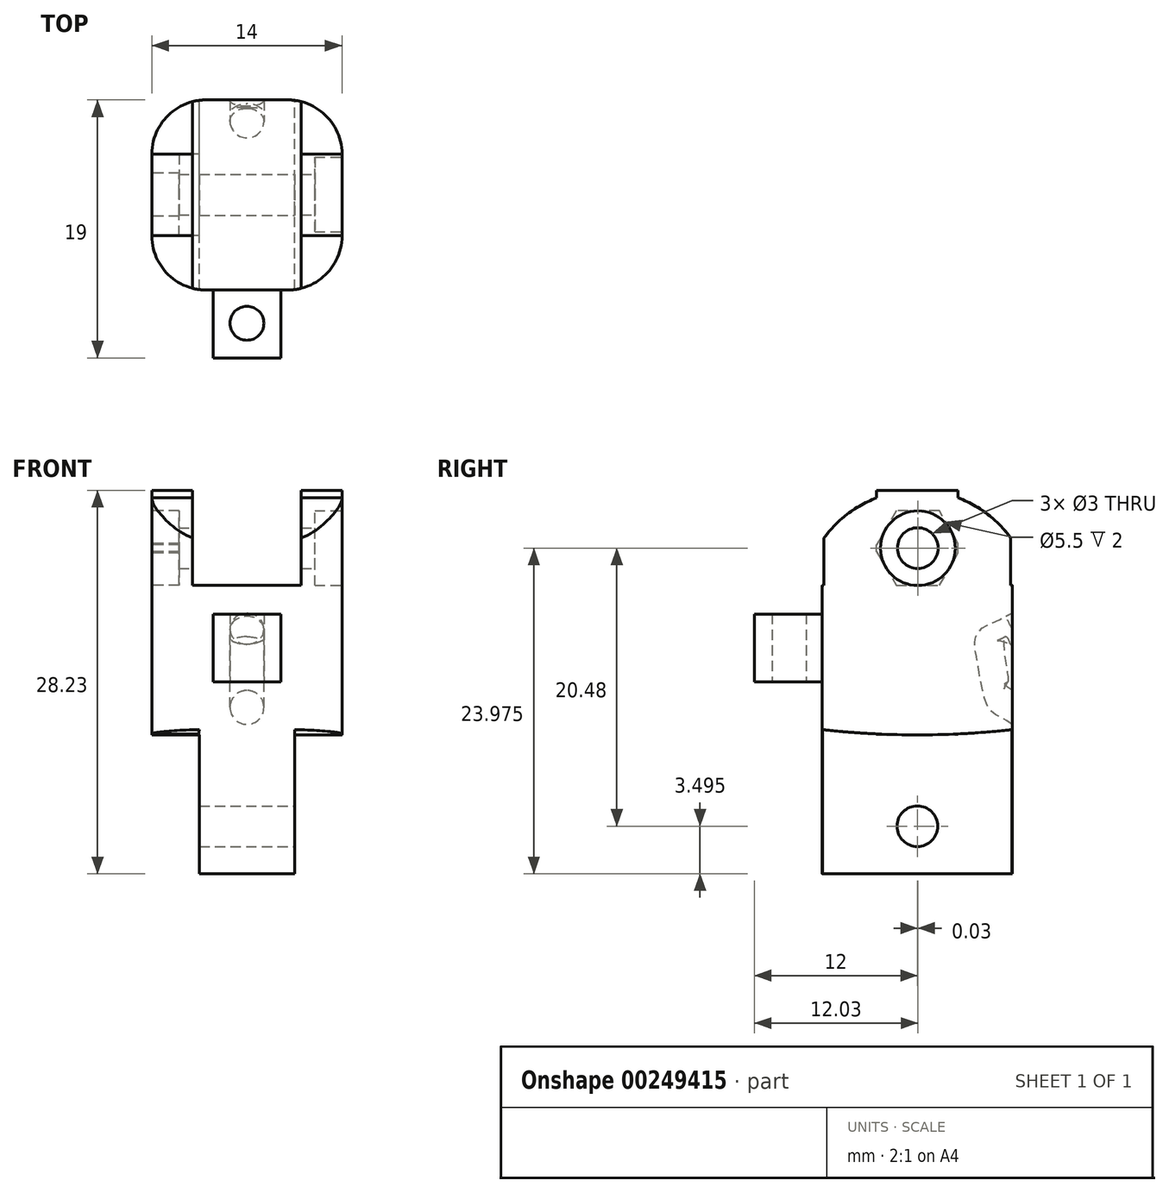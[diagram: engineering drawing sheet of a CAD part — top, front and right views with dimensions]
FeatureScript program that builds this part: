
annotation { "Feature Type Name" : "Feature", "Feature Type Description" : "" }
export const myFeature = defineFeature(function(context is Context, id is Id, definition is map)
    precondition{}
    {
        {
            var Q0;
            Q0=qCreatedBy(makeId("Front.planeOp"),FACE);
            var sketch = newSketch(context, id + "F0", { "sketchPlane" : qUnion([Q0])});
            skLineSegment(sketch, "E0.bottom", {"start": v(3.5, -14.12) * mm, "end": v(-3.5, -14.12) * mm});
            skLineSegment(sketch, "E0.top", {"start": v(7, 14.1) * mm, "end": v(4, 14.1) * mm});
            skLineSegment(sketch, "E0.left", {"start": v(7, -3.9) * mm, "end": v(7, 14.1) * mm});
            skLineSegment(sketch, "E0.right", {"start": v(-7, -3.9) * mm, "end": v(-7, 14.1) * mm});
            skPoint(sketch, "E0.middle", {"position": v(0, 0) * mm});
            skLineSegment(sketch, "E1.bottom", {"start": v(-3.5, -3.9) * mm, "end": v(-7, -3.9) * mm});
            skLineSegment(sketch, "E1.left", {"start": v(-3.5, -3.9) * mm, "end": v(-3.5, -14.12) * mm});
            skLineSegment(sketch, "E2.MirrorCS", {"start": v(3.5, -3.9) * mm, "end": v(7, -3.9) * mm});
            skLineSegment(sketch, "E3.MirrorCS", {"start": v(3.5, -3.9) * mm, "end": v(3.5, -14.12) * mm});
            skLineSegment(sketch, "E4.bottom", {"start": v(4, 7.1) * mm, "end": v(-4, 7.1) * mm});
            skLineSegment(sketch, "E4.left", {"start": v(4, 7.1) * mm, "end": v(4, 14.1) * mm});
            skLineSegment(sketch, "E4.right", {"start": v(-4, 7.1) * mm, "end": v(-4, 14.1) * mm});
            skLineSegment(sketch, "E5.trimOffspring", {"start": v(-4, 14.1) * mm, "end": v(-7, 14.1) * mm});
            skSolve(sketch);
        }
        {
            var Q0;
            Q0=makeQuery(id+"F0.imprint","IMPRINT",FACE,{"disambiguationData":[TD([[makeQuery(id+"F0.imprint","IMPRINT",EDGE,{"derivedFrom":sQuery(id+"F0.wireOp",EDGE,"E0.bottom")}),-1.0]])]});
            extrude(context, id + "F1", {"entities" : qUnion([Q0]), "depth" : 14 * mm});
        }
        {
            var Q0;
            Q0=makeQuery(id+"F1.opExtrude","CAP_EDGE",EDGE,{"disambiguationData":[OSD([sQuery(id+"F0.wireOp",EDGE,"E0.left")])],"isStart":true});
            var Q1;
            Q1=makeQuery(id+"F1.opExtrude","CAP_EDGE",EDGE,{"disambiguationData":[OSD([sQuery(id+"F0.wireOp",EDGE,"E0.right")])],"isStart":true});
            var Q2;
            Q2=makeQuery(id+"F1.opExtrude","CAP_EDGE",EDGE,{"disambiguationData":[OSD([sQuery(id+"F0.wireOp",EDGE,"E0.left")])],"isStart":false});
            var Q3;
            Q3=makeQuery(id+"F1.opExtrude","CAP_EDGE",EDGE,{"disambiguationData":[OSD([sQuery(id+"F0.wireOp",EDGE,"E0.right")])],"isStart":false});
            fillet(context, id + "F2", {"entities" : qUnion([Q0, Q1, Q2, Q3]), "radius" : 4 * mm, "tangentPropagation" : true, "allowEdgeOverflow" : false});
        }
        {
            var Q0;
            Q0=makeQuery(id+"F1.opExtrude","SWEPT_FACE",FACE,{"disambiguationData":[OSD([sQuery(id+"F0.wireOp",EDGE,"E0.left")])]});
            var sketch = newSketch(context, id + "F3", { "sketchPlane" : qUnion([Q0])});
            skCircle(sketch, "E6", {"center": v(-6.97, 9.86) * mm, "radius": 1.5 * mm});
            skCircle(sketch, "E7", {"center": v(-6.97, 9.86) * mm, "radius": 2.75 * mm});
            skSolve(sketch);
        }
        {
            var Q0;
            Q0=makeQuery(id+"F3.imprint","IMPRINT",FACE,{"disambiguationData":[TD([[makeQuery(id+"F3.imprint","IMPRINT",EDGE,{"derivedFrom":sQuery(id+"F3.wireOp",EDGE,"E6")}),1.0]])]});
            var Q1;
            Q1=sQuery(id+"F3.wireOp",EDGE,"E6");
            var Q2;
            Q2=makeQuery(id+"F1.opExtrude","SWEPT_FACE",FACE,{"disambiguationData":[OSD([sQuery(id+"F0.wireOp",EDGE,"E0.right")])]});
            extrude(context, id + "F4", {"entities" : qUnion([Q0]), "operationType" : NewBodyOperationType.REMOVE, "surfaceEntities" : qUnion([Q1]), "endBound" : BoundingType.UP_TO_SURFACE, "oppositeDirection" : true, "endBoundEntityFace" : qUnion([Q2]), "depth" : 25 * mm});
        }
        {
            var Q0;
            Q0=makeQuery(id+"F1.opExtrude","SWEPT_FACE",FACE,{"disambiguationData":[OSD([sQuery(id+"F0.wireOp",EDGE,"E3.MirrorCS")])]});
            var sketch = newSketch(context, id + "F5", { "sketchPlane" : qUnion([Q0])});
            skCircle(sketch, "E8", {"center": v(-7, -10.62) * mm, "radius": 1.5 * mm});
            skPoint(sketch, "E9.0", {"position": v(0, 0) * mm});
            skPoint(sketch, "E10.0", {"position": v(-0.03, -9) * mm});
            skSolve(sketch);
        }
        {
            var Q0;
            Q0=makeQuery(id+"F5.imprint","IMPRINT",FACE,{"disambiguationData":[TD([[makeQuery(id+"F5.imprint","IMPRINT",EDGE,{"derivedFrom":sQuery(id+"F5.wireOp",EDGE,"E8")}),1.0]])]});
            var Q1;
            Q1=makeQuery(id+"F1.opExtrude","SWEPT_FACE",FACE,{"disambiguationData":[OSD([sQuery(id+"F0.wireOp",EDGE,"E1.left")])]});
            extrude(context, id + "F6", {"entities" : qUnion([Q0]), "operationType" : NewBodyOperationType.REMOVE, "endBound" : BoundingType.UP_TO_SURFACE, "oppositeDirection" : true, "endBoundEntityFace" : qUnion([Q1]), "depth" : 25 * mm});
        }
        {
            var Q0;
            Q0=makeQuery(id+"F3.imprint","IMPRINT",FACE,{"disambiguationData":[TD([[makeQuery(id+"F3.imprint","IMPRINT",EDGE,{"derivedFrom":sQuery(id+"F3.wireOp",EDGE,"E6")}),-1.0]])]});
            var Q1;
            Q1=sQuery(id+"F3.wireOp",EDGE,"E7");
            extrude(context, id + "F7", {"entities" : qUnion([Q0]), "operationType" : NewBodyOperationType.REMOVE, "surfaceEntities" : qUnion([Q1]), "oppositeDirection" : true, "depth" : 2 * mm});
        }
        {
            var Q0;
            Q0=makeQuery(id+"F3.imprint","IMPRINT",FACE,{"disambiguationData":[TD([[makeQuery(id+"F3.imprint","IMPRINT",EDGE,{"derivedFrom":sQuery(id+"F3.wireOp",EDGE,"E7")}),-1.0]])]});
            var sketch = newSketch(context, id + "F8", { "sketchPlane" : qUnion([Q0])});
            skPoint(sketch, "E11.0", {"position": v(-0.13, 14.1) * mm});
            skPoint(sketch, "E12.0", {"position": v(-13.87, 14.1) * mm});
            skPoint(sketch, "E13.0", {"position": v(-0.13, 10.6) * mm});
            skPoint(sketch, "E14.0", {"position": v(-13.87, 10.6) * mm});
            skArc(sketch, "E15", {"start": v(-0.13, 10.6) * mm, "mid": v(-7, 14.1) * mm, "end": v(-13.87, 10.6) * mm});
            skPoint(sketch, "E16.0", {"position": v(-7, 14.1) * mm});
            skLineSegment(sketch, "E17", {"start": v(-13.87, 10.6) * mm, "end": v(-13.87, 14.1) * mm});
            skLineSegment(sketch, "E18", {"start": v(-13.87, 14.1) * mm, "end": v(-7, 14.1) * mm});
            skLineSegment(sketch, "E19", {"start": v(-7, 14.1) * mm, "end": v(-0.13, 14.1) * mm});
            skLineSegment(sketch, "E20", {"start": v(-0.13, 14.1) * mm, "end": v(-0.13, 10.6) * mm});
            skSolve(sketch);
        }
        {
            var Q0;
            Q0=makeQuery(id+"F1.opExtrude","SWEPT_FACE",FACE,{"disambiguationData":[OSD([sQuery(id+"F0.wireOp",EDGE,"E0.right")])]});
            var sketch = newSketch(context, id + "F9", { "sketchPlane" : qUnion([Q0])});
            skCircle(sketch, "E21.cCircle", {"center": v(6.97, 9.86) * mm, "radius": 2.75 * mm, "construction": true});
            skLineSegment(sketch, "E21.0", {"start": v(5.38, 12.6) * mm, "end": v(8.56, 12.6) * mm});
            skLineSegment(sketch, "E21.1", {"start": v(8.56, 12.6) * mm, "end": v(10.15, 9.86) * mm});
            skLineSegment(sketch, "E21.2", {"start": v(10.15, 9.86) * mm, "end": v(8.56, 7.1) * mm});
            skLineSegment(sketch, "E21.3", {"start": v(8.56, 7.1) * mm, "end": v(5.38, 7.1) * mm});
            skLineSegment(sketch, "E21.4", {"start": v(5.38, 7.1) * mm, "end": v(3.8, 9.86) * mm});
            skLineSegment(sketch, "E21.5", {"start": v(3.8, 9.86) * mm, "end": v(5.38, 12.6) * mm});
            skPoint(sketch, "E21.0.midPoint", {"position": v(6.97, 12.6) * mm});
            skSolve(sketch);
        }
        {
            var Q0;
            {var subQ13=sQuery(id+"F9.wireOp",EDGE,"E21.0");Q0=makeQuery(id+"F9.imprint","IMPRINT",FACE,{"disambiguationData":[TD([[makeQuery(id+"F9.imprint","IMPRINT",EDGE,{"derivedFrom":subQ13}),-1.0]])]});}
            extrude(context, id + "F10", {"entities" : qUnion([Q0]), "operationType" : NewBodyOperationType.REMOVE, "oppositeDirection" : true, "depth" : 2 * mm});
        }
        {
            var Q0;
            {var subQ0=sQuery(id+"F8.wireOp",EDGE,"E17");Q0=makeQuery(id+"F8.imprint","IMPRINT",FACE,{"disambiguationData":[TD([[makeQuery(id+"F8.imprint","IMPRINT",EDGE,{"derivedFrom":subQ0}),-1.0]])]});}
            var Q1;
            {var subQ0=sQuery(id+"F8.wireOp",EDGE,"E18");var subQ1=sQuery(id+"F8.wireOp",EDGE,"E15");var subQ2=makeQuery(id+"F8.imprint","INTERSECT",VERTEX,{"derivedFrom":[subQ1,subQ0,sQuery(id+"F8.wireOp",EDGE,"E19")]});Q1=makeQuery(id+"F8.imprint","IMPRINT",FACE,{"disambiguationData":[TD([[makeQuery(id+"F8.imprint","IMPRINT",EDGE,{"disambiguationData":[TD([[subQ2,-1.0]])],"derivedFrom":subQ1}),-1.0]])]});}
            var Q2;
            {var subQ0=sQuery(id+"F8.wireOp",EDGE,"E19");var subQ1=sQuery(id+"F8.wireOp",EDGE,"E15");var subQ2=makeQuery(id+"F8.imprint","INTERSECT",VERTEX,{"derivedFrom":[subQ1,sQuery(id+"F8.wireOp",EDGE,"E18"),subQ0]});Q2=makeQuery(id+"F8.imprint","IMPRINT",FACE,{"disambiguationData":[TD([[makeQuery(id+"F8.imprint","IMPRINT",EDGE,{"disambiguationData":[TD([[subQ2,1.0]])],"derivedFrom":subQ1}),-1.0]])]});}
            var Q3;
            {var subQ0=sQuery(id+"F8.wireOp",EDGE,"E20");Q3=makeQuery(id+"F8.imprint","IMPRINT",FACE,{"disambiguationData":[TD([[makeQuery(id+"F8.imprint","IMPRINT",EDGE,{"derivedFrom":subQ0}),-1.0]])]});}
            var Q4;
            {var subQ0=sQuery(id+"F0.wireOp",EDGE,"E0.right");var subQ5=makeQuery(id+"F1.opExtrude","SWEPT_FACE",FACE,{"disambiguationData":[OSD([subQ0])]});Q4=makeQuery(id+"F10.boolean.opBoolean","SPLIT",FACE,{"disambiguationData":[TD([makeQuery(id+"F1.opExtrude","SWEPT_FACE",FACE,{"disambiguationData":[OSD([sQuery(id+"F0.wireOp",EDGE,"E5.trimOffspring")])]})])],"derivedFrom":subQ5});}
            extrude(context, id + "F11", {"entities" : qUnion([Q0, Q1, Q2, Q3]), "operationType" : NewBodyOperationType.REMOVE, "endBound" : BoundingType.UP_TO_SURFACE, "oppositeDirection" : true, "endBoundEntityFace" : qUnion([Q4]), "depth" : 25 * mm});
        }
        {
            var Q0;
            Q0=makeQuery(id+"F3.imprint","IMPRINT",FACE,{"disambiguationData":[TD([[makeQuery(id+"F3.imprint","IMPRINT",EDGE,{"derivedFrom":sQuery(id+"F3.wireOp",EDGE,"E7")}),-1.0]])]});
            var sketch = newSketch(context, id + "F12", { "sketchPlane" : qUnion([Q0])});
            skLineSegment(sketch, "E22.0", {"start": v(-13.97, -14.12) * mm, "end": v(-0.03, -14.12) * mm});
            skEllipticalArc(sketch, "E23.0", {});
            skLineSegment(sketch, "E24.0", {"start": v(0, 7.1) * mm, "end": v(0, -14.12) * mm});
            skEllipticalArc(sketch, "E25.0", {});
            skLineSegment(sketch, "E26.0", {"start": v(-14, -14.12) * mm, "end": v(-14, 7.1) * mm});
            skPoint(sketch, "E27.0", {"position": v(0, -3.5) * mm});
            skPoint(sketch, "E28.0", {"position": v(-14, -3.5) * mm});
            skPoint(sketch, "E29.0", {"position": v(-7, -3.9) * mm});
            skArc(sketch, "E30", {"start": v(-14, -3.5) * mm, "mid": v(-7, -3.9) * mm, "end": v(0, -3.5) * mm});
            skLineSegment(sketch, "E31", {"start": v(-13.97, -3.9) * mm, "end": v(-14, -3.5) * mm});
            skLineSegment(sketch, "E32", {"start": v(-0.03, -3.9) * mm, "end": v(0, -3.5) * mm});
            skLineSegment(sketch, "E33.0", {"start": v(-10, 13.56) * mm, "end": v(-10, -3.82) * mm});
            skLineSegment(sketch, "E34.0", {"start": v(-4, -3.82) * mm, "end": v(-4, 13.56) * mm});
            skLineSegment(sketch, "E35", {"start": v(-0.03, -3.9) * mm, "end": v(-0.03, -7.8) * mm});
            skLineSegment(sketch, "E36", {"start": v(-13.97, -3.9) * mm, "end": v(-13.95, -7.8) * mm});
            skLineSegment(sketch, "E37", {"start": v(-13.95, -7.8) * mm, "end": v(-0.03, -7.8) * mm});
            skLineSegment(sketch, "E38", {"start": v(0, -3.5) * mm, "end": v(-0.03, -7.8) * mm});
            skLineSegment(sketch, "E39", {"start": v(-14, -3.5) * mm, "end": v(-13.95, -7.8) * mm});
            skPoint(sketch, "E40.orphan", {"position": v(-4, -3.9) * mm});
            skPoint(sketch, "E41.orphan", {"position": v(-10, -3.9) * mm});
            const initialGuessF12  = {"E23.0": [-0.01, -0.053958912450485556, 0, -1, 0.3190356408007645, 0.004, 4.564913868686836, 4.587061149216624], "E25.0": [-0.004, -0.05395891245048557, 0, 1, 0.3190356408007645, 0.004, 4.837716811552756, 4.859864092082543]};
            skSetInitialGuess(sketch, initialGuessF12);
            skSolve(sketch);
        }
        {
            var Q0;
            {var subQ11=sQuery(id+"F12.wireOp",EDGE,"E31");Q0=makeQuery(id+"F12.imprint","IMPRINT",FACE,{"disambiguationData":[TD([[makeQuery(id+"F12.imprint","IMPRINT",EDGE,{"derivedFrom":subQ11}),-1.0]])]});}
            var Q1;
            {var subQ0=sQuery(id+"F12.wireOp",EDGE,"E30");var subQ1=sQuery(id+"F0.wireOp",EDGE,"E0.left");var subQ4=makeQuery(id+"F3.imprint","IMPRINT",EDGE,{"derivedFrom":makeQuery(id+"F1.opExtrude","SWEPT_EDGE",EDGE,{"disambiguationData":[OSD([sQuery(id+"F0.wireOp",EDGE,"E2.MirrorCS"),subQ1])]})});var subQ5=makeQuery(id+"F12.imprint","INTERSECT",VERTEX,{"derivedFrom":[subQ4,subQ0]});Q1=makeQuery(id+"F12.imprint","IMPRINT",FACE,{"disambiguationData":[TD([[makeQuery(id+"F12.imprint","IMPRINT",EDGE,{"disambiguationData":[TD([[subQ5,1.0]])],"derivedFrom":subQ0}),-1.0]])]});}
            var Q2;
            {var subQ0=sQuery(id+"F12.wireOp",EDGE,"E30");var subQ1=sQuery(id+"F0.wireOp",EDGE,"E0.left");var subQ4=makeQuery(id+"F3.imprint","IMPRINT",EDGE,{"derivedFrom":makeQuery(id+"F1.opExtrude","SWEPT_EDGE",EDGE,{"disambiguationData":[OSD([sQuery(id+"F0.wireOp",EDGE,"E2.MirrorCS"),subQ1])]})});var subQ5=makeQuery(id+"F12.imprint","INTERSECT",VERTEX,{"derivedFrom":[subQ4,subQ0]});Q2=makeQuery(id+"F12.imprint","IMPRINT",FACE,{"disambiguationData":[TD([[makeQuery(id+"F12.imprint","IMPRINT",EDGE,{"disambiguationData":[TD([[subQ5,-1.0]])],"derivedFrom":subQ0}),-1.0]])]});}
            var Q3;
            Q3=makeQuery(id+"F1.opExtrude","SWEPT_FACE",FACE,{"disambiguationData":[OSD([sQuery(id+"F0.wireOp",EDGE,"E3.MirrorCS")])]});
            extrude(context, id + "F13", {"entities" : qUnion([Q0, Q1, Q2]), "operationType" : NewBodyOperationType.REMOVE, "endBound" : BoundingType.UP_TO_SURFACE, "oppositeDirection" : true, "endBoundEntityFace" : qUnion([Q3]), "depth" : 25 * mm});
        }
        {
            var Q0;
            {var subQ1=sQuery(id+"F0.wireOp",EDGE,"E0.right");var subQ5=makeQuery(id+"F1.opExtrude","SWEPT_FACE",FACE,{"disambiguationData":[OSD([subQ1])]});Q0=makeQuery(id+"F10.boolean.opBoolean","SPLIT",FACE,{"disambiguationData":[TD([makeQuery(id+"F1.opExtrude","SWEPT_FACE",FACE,{"disambiguationData":[OSD([sQuery(id+"F0.wireOp",EDGE,"E1.bottom")])]})])],"derivedFrom":subQ5});}
            var sketch = newSketch(context, id + "F14", { "sketchPlane" : qUnion([Q0])});
            skArc(sketch, "E42.0", {"start": v(13.97, -3.51) * mm, "mid": v(11.99, -3.7) * mm, "end": v(10, -3.82) * mm});
            skArc(sketch, "E43.0", {"start": v(10, -3.82) * mm, "mid": v(7, -3.9) * mm, "end": v(4, -3.82) * mm});
            skArc(sketch, "E44.0", {"start": v(4, -3.82) * mm, "mid": v(2.01, -3.7) * mm, "end": v(0.03, -3.51) * mm});
            skArc(sketch, "E45", {"start": v(13.97, -3.51) * mm, "mid": v(7, -3.9) * mm, "end": v(0.03, -3.51) * mm});
            skLineSegment(sketch, "E46", {"start": v(7, -3.9) * mm, "end": v(0, -3.9) * mm});
            skLineSegment(sketch, "E47", {"start": v(0, -3.9) * mm, "end": v(0.03, -3.51) * mm});
            skLineSegment(sketch, "E48", {"start": v(7, -3.9) * mm, "end": v(13.96, -3.9) * mm});
            skLineSegment(sketch, "E49", {"start": v(13.96, -3.9) * mm, "end": v(13.97, -3.51) * mm});
            skSolve(sketch);
        }
        {
            var Q0;
            {var subQ0=sQuery(id+"F14.wireOp",EDGE,"E47");Q0=makeQuery(id+"F14.imprint","IMPRINT",FACE,{"disambiguationData":[TD([[makeQuery(id+"F14.imprint","IMPRINT",EDGE,{"derivedFrom":subQ0}),-1.0]])]});}
            var Q1;
            {var subQ0=sQuery(id+"F14.wireOp",EDGE,"E46");var subQ1=sQuery(id+"F14.wireOp",EDGE,"E45");var subQ2=makeQuery(id+"F14.imprint","INTERSECT",VERTEX,{"derivedFrom":[subQ1,subQ0,sQuery(id+"F14.wireOp",EDGE,"E48")]});Q1=makeQuery(id+"F14.imprint","IMPRINT",FACE,{"disambiguationData":[TD([[makeQuery(id+"F14.imprint","IMPRINT",EDGE,{"disambiguationData":[TD([[subQ2,-1.0]])],"derivedFrom":subQ1}),1.0]])]});}
            var Q2;
            {var subQ0=sQuery(id+"F14.wireOp",EDGE,"E48");var subQ1=sQuery(id+"F14.wireOp",EDGE,"E45");var subQ2=makeQuery(id+"F14.imprint","INTERSECT",VERTEX,{"derivedFrom":[subQ1,sQuery(id+"F14.wireOp",EDGE,"E46"),subQ0]});Q2=makeQuery(id+"F14.imprint","IMPRINT",FACE,{"disambiguationData":[TD([[makeQuery(id+"F14.imprint","IMPRINT",EDGE,{"disambiguationData":[TD([[subQ2,1.0]])],"derivedFrom":subQ1}),1.0]])]});}
            var Q3;
            {var subQ0=sQuery(id+"F14.wireOp",EDGE,"E49");Q3=makeQuery(id+"F14.imprint","IMPRINT",FACE,{"disambiguationData":[TD([[makeQuery(id+"F14.imprint","IMPRINT",EDGE,{"derivedFrom":subQ0}),1.0]])]});}
            var Q4;
            Q4=makeQuery(id+"F1.opExtrude","SWEPT_FACE",FACE,{"disambiguationData":[OSD([sQuery(id+"F0.wireOp",EDGE,"E1.left")])]});
            extrude(context, id + "F15", {"entities" : qUnion([Q0, Q1, Q2, Q3]), "operationType" : NewBodyOperationType.REMOVE, "endBound" : BoundingType.UP_TO_SURFACE, "oppositeDirection" : true, "endBoundEntityFace" : qUnion([Q4]), "depth" : 25 * mm});
        }
        {
            var Q0;
            Q0=makeQuery(id+"F1.opExtrude","CAP_FACE",FACE,{"disambiguationData":[OSD([sQuery(id+"F0.wireOp",EDGE,"E0.bottom"),sQuery(id+"F0.wireOp",EDGE,"E0.top"),sQuery(id+"F0.wireOp",EDGE,"E0.right"),sQuery(id+"F0.wireOp",EDGE,"E1.bottom"),sQuery(id+"F0.wireOp",EDGE,"E1.left"),sQuery(id+"F0.wireOp",EDGE,"E2.MirrorCS"),sQuery(id+"F0.wireOp",EDGE,"E3.MirrorCS"),sQuery(id+"F0.wireOp",EDGE,"E0.left"),sQuery(id+"F0.wireOp",EDGE,"E4.bottom"),sQuery(id+"F0.wireOp",EDGE,"E4.left"),sQuery(id+"F0.wireOp",EDGE,"E4.right"),sQuery(id+"F0.wireOp",EDGE,"E5.trimOffspring")])],"isStart":true});
            var sketch = newSketch(context, id + "F16", { "sketchPlane" : qUnion([Q0])});
            skCircle(sketch, "E50", {"center": v(0, 3.86) * mm, "radius": 1.25 * mm});
            skCircle(sketch, "E51", {"center": v(0, -1.87) * mm, "radius": 1.25 * mm});
            skSolve(sketch);
        }
        {
            var Q0;
            Q0=qCreatedBy(makeId("Right.planeOp"),FACE);
            var sketch = newSketch(context, id + "F17", { "sketchPlane" : qUnion([Q0])});
            skFitSpline(sketch, "E52", {"points": [v(0, 3.85) * mm, v(-1.57, 2.6) * mm, v(-1.03, -0.77) * mm, v(0, -1.82) * mm], "startDerivative": vector(-13.13, -6.04) * mm, "endDerivative": vector(8.15, -5.56) * mm});
            skLineSegment(sketch, "E53", {"start": v(0, 3.85) * mm, "end": v(1.98, 4.85) * mm});
            skLineSegment(sketch, "E54", {"start": v(0, -1.82) * mm, "end": v(1.73, -2.3) * mm});
            skSolve(sketch);
        }
        {
            var Q0;
            Q0=makeQuery(id+"F16.imprint","IMPRINT",FACE,{"disambiguationData":[TD([[makeQuery(id+"F16.imprint","IMPRINT",EDGE,{"derivedFrom":sQuery(id+"F16.wireOp",EDGE,"E51")}),1.0]])]});
            var Q1;
            Q1=sQuery(id+"F17.wireOp",EDGE,"E52");
            var Q2;
            Q2=sQuery(id+"F17.wireOp",EDGE,"E53");
            sweep(context, id + "F18", {"operationType" : NewBodyOperationType.REMOVE, "profiles" : qUnion([Q0]), "path" : qUnion([Q1, Q2])});
        }
        {
            var Q0;
            Q0=qCreatedBy(makeId("Top.planeOp"),FACE);
            var sketch = newSketch(context, id + "F19", { "sketchPlane" : qUnion([Q0])});
            skLineSegment(sketch, "E55.bottom", {"start": v(-2.5, -19) * mm, "end": v(2.5, -19) * mm});
            skLineSegment(sketch, "E55.top", {"start": v(-2.5, -14) * mm, "end": v(2.5, -14) * mm});
            skLineSegment(sketch, "E55.left", {"start": v(-2.5, -19) * mm, "end": v(-2.5, -14) * mm});
            skLineSegment(sketch, "E55.right", {"start": v(2.5, -19) * mm, "end": v(2.5, -14) * mm});
            skPoint(sketch, "E56", {"position": v(0, -16.45) * mm});
            skCircle(sketch, "E57", {"center": v(0, -16.45) * mm, "radius": 1.25 * mm});
            skSolve(sketch);
        }
        {
            var Q0;
            Q0=makeQuery(id+"F19.imprint","IMPRINT",FACE,{"disambiguationData":[TD([[makeQuery(id+"F19.imprint","IMPRINT",EDGE,{"derivedFrom":sQuery(id+"F19.wireOp",EDGE,"E55.bottom")}),1.0]])]});
            extrude(context, id + "F20", {"entities" : qUnion([Q0]), "operationType" : NewBodyOperationType.ADD, "depth" : 5 * mm});
        }
    });
